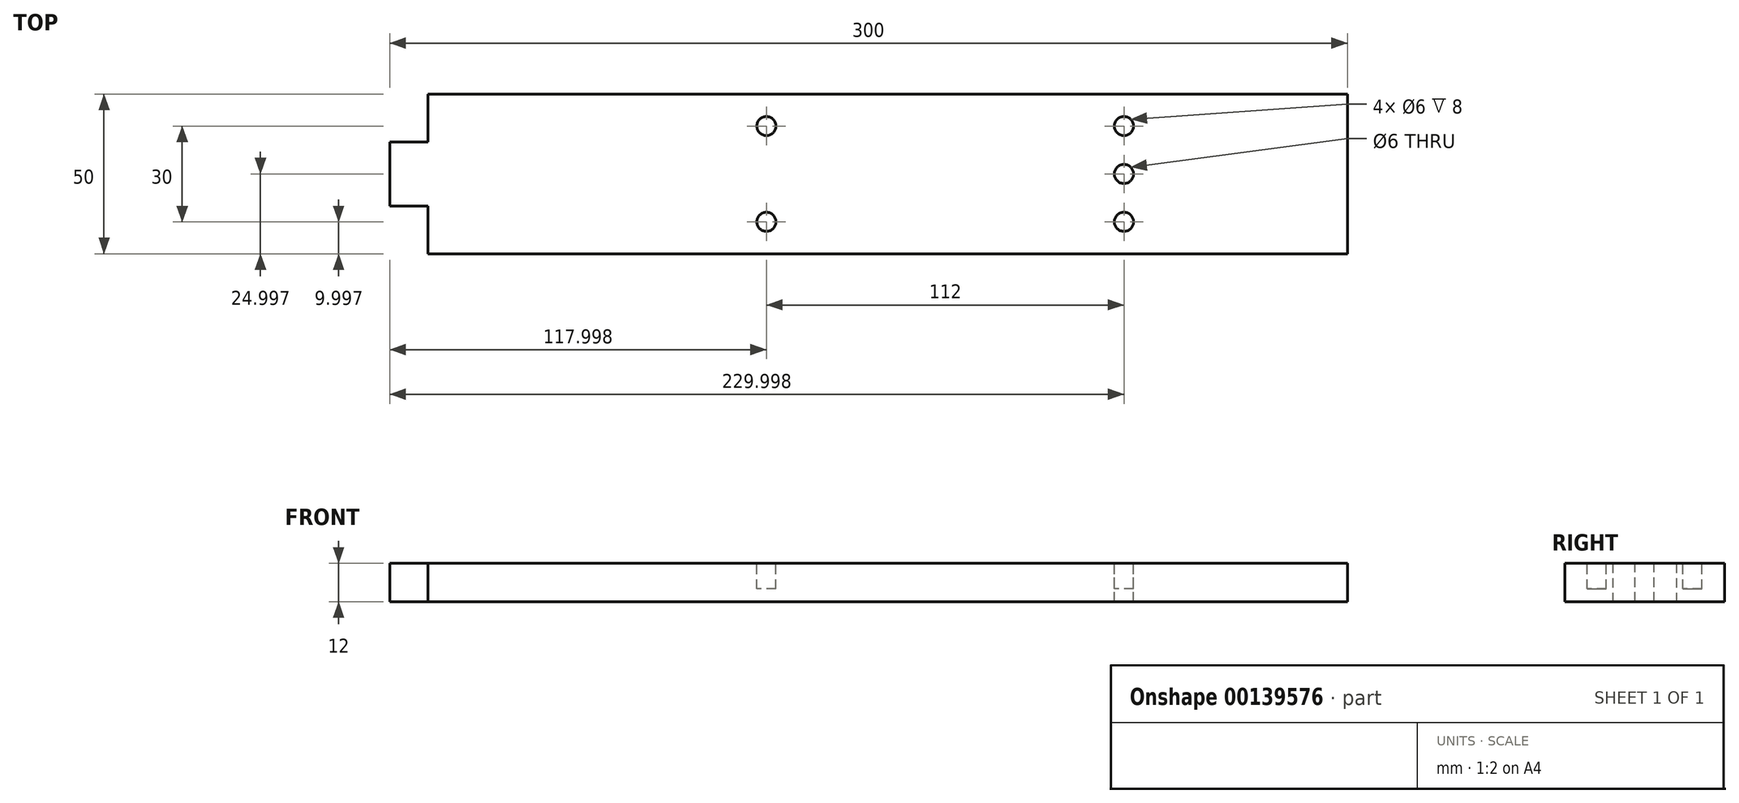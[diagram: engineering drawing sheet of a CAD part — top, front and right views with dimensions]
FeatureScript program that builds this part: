
annotation { "Feature Type Name" : "Feature", "Feature Type Description" : "" }
export const myFeature = defineFeature(function(context is Context, id is Id, definition is map)
    precondition{}
    {
        {
            var Q0;
            Q0=qCreatedBy(makeId("Top.planeOp"),FACE);
            var sketch = newSketch(context, id + "F0", { "sketchPlane" : qUnion([Q0])});
            skLineSegment(sketch, "E0.bottom", {"start": v(-151.82, 23) * mm, "end": v(148.18, 23) * mm});
            skLineSegment(sketch, "E0.top", {"start": v(-151.82, -27) * mm, "end": v(148.18, -27) * mm});
            skLineSegment(sketch, "E0.left", {"start": v(-151.82, 23) * mm, "end": v(-151.82, -27) * mm});
            skLineSegment(sketch, "E0.right", {"start": v(148.18, 23) * mm, "end": v(148.18, -27) * mm});
            skSolve(sketch);
        }
        {
            var Q0;
            Q0 = qSketchRegion(id + "F0", true);
            extrude(context, id + "F1", {"entities" : qUnion([Q0]), "depth" : 12 * mm});
        }
        {
            var Q0;
            Q0=makeQuery(id+"F1.opExtrude","CAP_FACE",FACE,{"disambiguationData":[OSD([sQuery(id+"F0.wireOp",EDGE,"E0.bottom"),sQuery(id+"F0.wireOp",EDGE,"E0.top"),sQuery(id+"F0.wireOp",EDGE,"E0.left"),sQuery(id+"F0.wireOp",EDGE,"E0.right")])],"isStart":false});
            var sketch = newSketch(context, id + "F2", { "sketchPlane" : qUnion([Q0])});
            skLineSegment(sketch, "E1.bottom", {"start": v(-151.82, 23) * mm, "end": v(-139.82, 23) * mm});
            skLineSegment(sketch, "E1.top", {"start": v(-151.82, 8) * mm, "end": v(-139.82, 8) * mm});
            skLineSegment(sketch, "E1.left", {"start": v(-151.82, 23) * mm, "end": v(-151.82, 8) * mm});
            skLineSegment(sketch, "E1.right", {"start": v(-139.82, 23) * mm, "end": v(-139.82, 8) * mm});
            skLineSegment(sketch, "E2.bottom", {"start": v(-151.82, -27) * mm, "end": v(-139.82, -27) * mm});
            skLineSegment(sketch, "E2.top", {"start": v(-151.82, -12) * mm, "end": v(-139.82, -12) * mm});
            skLineSegment(sketch, "E2.left", {"start": v(-151.82, -27) * mm, "end": v(-151.82, -12) * mm});
            skLineSegment(sketch, "E2.right", {"start": v(-139.82, -27) * mm, "end": v(-139.82, -12) * mm});
            skSolve(sketch);
        }
        {
            var Q0;
            Q0=makeQuery(id+"F2.imprint","IMPRINT",FACE,{"disambiguationData":[TD([[makeQuery(id+"F2.imprint","IMPRINT",EDGE,{"derivedFrom":sQuery(id+"F2.wireOp",EDGE,"E1.bottom")}),-1.0]])]});
            var Q1;
            Q1=makeQuery(id+"F2.imprint","IMPRINT",FACE,{"disambiguationData":[TD([[makeQuery(id+"F2.imprint","IMPRINT",EDGE,{"derivedFrom":sQuery(id+"F2.wireOp",EDGE,"E2.bottom")}),1.0]])]});
            extrude(context, id + "F3", {"entities" : qUnion([Q0, Q1]), "operationType" : NewBodyOperationType.REMOVE, "depth" : 25 * mm, "symmetric" : true});
        }
        {
            var Q0;
            Q0=makeQuery(id+"F1.opExtrude","CAP_FACE",FACE,{"disambiguationData":[OSD([sQuery(id+"F0.wireOp",EDGE,"E0.bottom"),sQuery(id+"F0.wireOp",EDGE,"E0.top"),sQuery(id+"F0.wireOp",EDGE,"E0.left"),sQuery(id+"F0.wireOp",EDGE,"E0.right")])],"isStart":false});
            var sketch = newSketch(context, id + "F4", { "sketchPlane" : qUnion([Q0])});
            skCircle(sketch, "E3", {"center": v(-33.82, 13) * mm, "radius": 3 * mm});
            skCircle(sketch, "E4", {"center": v(-33.82, -17) * mm, "radius": 3 * mm});
            skCircle(sketch, "E5", {"center": v(78.18, 13) * mm, "radius": 3 * mm});
            skCircle(sketch, "E6", {"center": v(78.18, -17) * mm, "radius": 3 * mm});
            skSolve(sketch);
        }
        {
            var Q0;
            Q0=makeQuery(id+"F4.imprint","IMPRINT",FACE,{"disambiguationData":[TD([[makeQuery(id+"F4.imprint","IMPRINT",EDGE,{"derivedFrom":sQuery(id+"F4.wireOp",EDGE,"E4")}),1.0]])]});
            var Q1;
            Q1=makeQuery(id+"F4.imprint","IMPRINT",FACE,{"disambiguationData":[TD([[makeQuery(id+"F4.imprint","IMPRINT",EDGE,{"derivedFrom":sQuery(id+"F4.wireOp",EDGE,"E5")}),1.0]])]});
            var Q2;
            Q2=makeQuery(id+"F4.imprint","IMPRINT",FACE,{"disambiguationData":[TD([[makeQuery(id+"F4.imprint","IMPRINT",EDGE,{"derivedFrom":sQuery(id+"F4.wireOp",EDGE,"E6")}),1.0]])]});
            var Q3;
            Q3=makeQuery(id+"F4.imprint","IMPRINT",FACE,{"disambiguationData":[TD([[makeQuery(id+"F4.imprint","IMPRINT",EDGE,{"derivedFrom":sQuery(id+"F4.wireOp",EDGE,"E3")}),1.0]])]});
            extrude(context, id + "F5", {"entities" : qUnion([Q0, Q1, Q2, Q3]), "operationType" : NewBodyOperationType.REMOVE, "oppositeDirection" : true, "depth" : 8 * mm});
        }
        {
            var Q0;
            Q0=makeQuery(id+"F1.opExtrude","CAP_FACE",FACE,{"disambiguationData":[OSD([sQuery(id+"F0.wireOp",EDGE,"E0.bottom"),sQuery(id+"F0.wireOp",EDGE,"E0.top"),sQuery(id+"F0.wireOp",EDGE,"E0.left"),sQuery(id+"F0.wireOp",EDGE,"E0.right")])],"isStart":false});
            var sketch = newSketch(context, id + "F6", { "sketchPlane" : qUnion([Q0])});
            skCircle(sketch, "E7", {"center": v(78.18, -2) * mm, "radius": 3 * mm});
            skSolve(sketch);
        }
        {
            var Q0;
            Q0=makeQuery(id+"F6.imprint","IMPRINT",FACE,{"disambiguationData":[TD([[makeQuery(id+"F6.imprint","IMPRINT",EDGE,{"derivedFrom":sQuery(id+"F6.wireOp",EDGE,"E7")}),1.0]])]});
            extrude(context, id + "F7", {"entities" : qUnion([Q0]), "operationType" : NewBodyOperationType.REMOVE, "endBound" : BoundingType.THROUGH_ALL, "oppositeDirection" : true, "depth" : 25 * mm});
        }
    });
